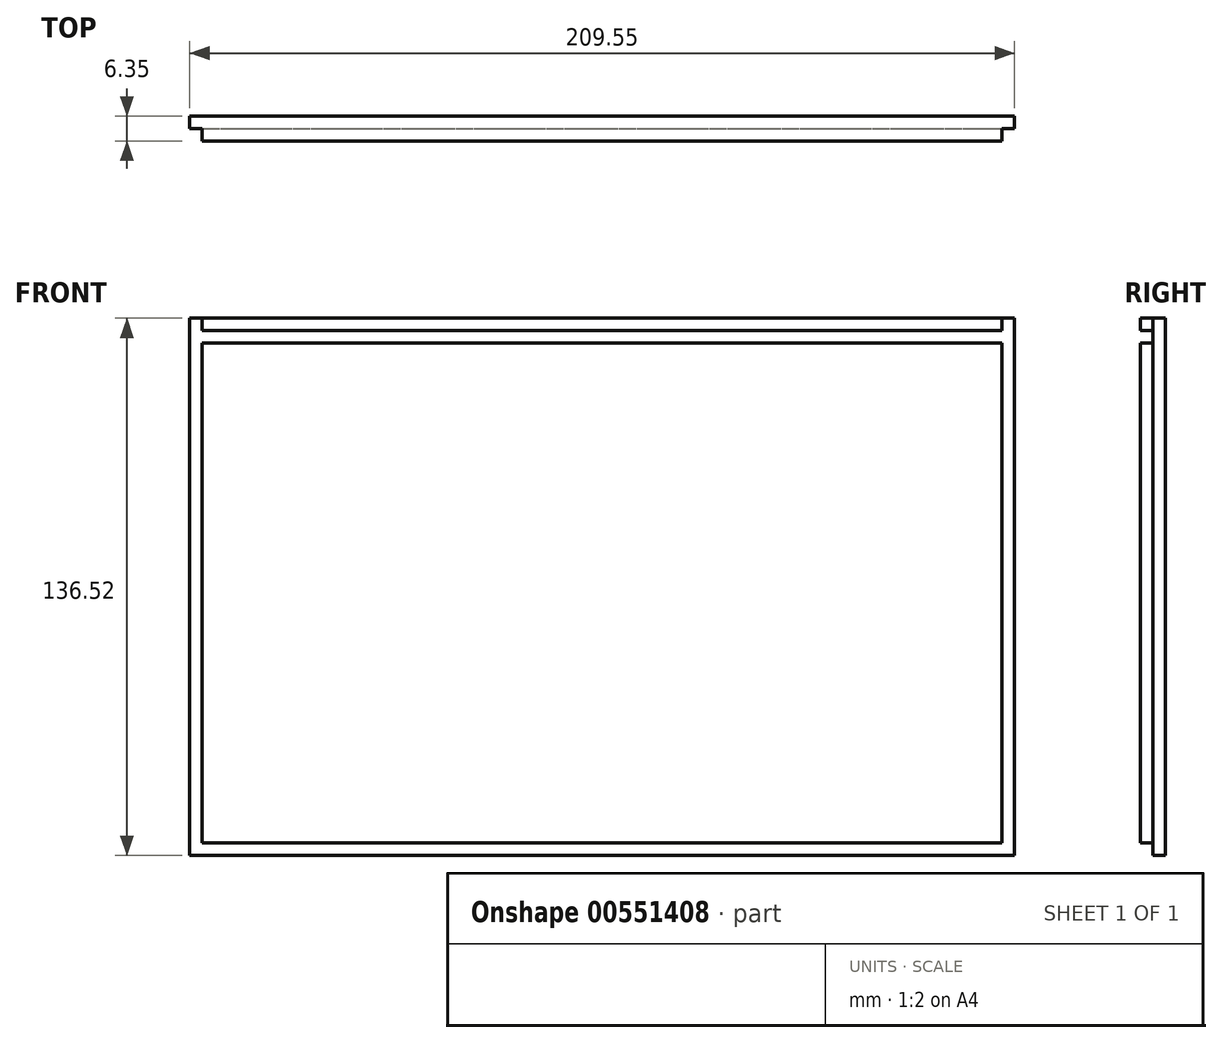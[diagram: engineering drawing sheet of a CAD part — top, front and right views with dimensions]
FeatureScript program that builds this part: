
annotation { "Feature Type Name" : "Feature", "Feature Type Description" : "" }
export const myFeature = defineFeature(function(context is Context, id is Id, definition is map)
    precondition{}
    {
        {
            var Q0;
            Q0=qCreatedBy(makeId("Front.planeOp"),FACE);
            var sketch = newSketch(context, id + "F0", { "sketchPlane" : qUnion([Q0])});
            skLineSegment(sketch, "E0.bottom", {"start": v(101.6, 63.5) * mm, "end": v(-101.6, 63.5) * mm});
            skLineSegment(sketch, "E0.top", {"start": v(101.6, -63.5) * mm, "end": v(-101.6, -63.5) * mm});
            skLineSegment(sketch, "E0.left", {"start": v(101.6, 63.5) * mm, "end": v(101.6, -63.5) * mm});
            skLineSegment(sketch, "E0.right", {"start": v(-101.6, 63.5) * mm, "end": v(-101.6, -63.5) * mm});
            skPoint(sketch, "E0.middle", {"position": v(0, 0) * mm});
            skPoint(sketch, "E1.endSnap0", {"position": v(-101.6, 0) * mm});
            skPoint(sketch, "E2.endSnap0", {"position": v(0, 63.5) * mm});
            skPoint(sketch, "E3.endSnap0", {"position": v(0, -63.5) * mm});
            skSolve(sketch);
        }
        {
            var Q0;
            Q0 = qSketchRegion(id + "F0", true);
            extrude(context, id + "F1", {"entities" : qUnion([Q0]), "depth" : 6.35 * mm, "offsetDistance" : 25.4 * mm});
        }
        {
            var Q0;
            Q0=makeQuery(id+"F1.opExtrude","SWEPT_FACE",FACE,{"disambiguationData":[OSD([sQuery(id+"F0.wireOp",EDGE,"E0.left")])]});
            var sketch = newSketch(context, id + "F2", { "sketchPlane" : qUnion([Q0])});
            skLineSegment(sketch, "E4", {"start": v(0, 63.5) * mm, "end": v(-3.18, 63.5) * mm});
            skLineSegment(sketch, "E5", {"start": v(-3.18, 63.5) * mm, "end": v(-3.18, 66.68) * mm});
            skLineSegment(sketch, "E6", {"start": v(-3.18, 66.68) * mm, "end": v(-6.35, 66.68) * mm});
            skLineSegment(sketch, "E7", {"start": v(-6.35, 66.68) * mm, "end": v(-6.35, 69.85) * mm});
            skLineSegment(sketch, "E8", {"start": v(-6.35, 69.85) * mm, "end": v(0, 69.85) * mm});
            skLineSegment(sketch, "E9", {"start": v(0, 69.85) * mm, "end": v(0, 63.5) * mm});
            skLineSegment(sketch, "E10", {"start": v(-30.08, 0) * mm, "end": v(17.13, 0) * mm, "construction": true});
            skPoint(sketch, "E10.endSnap0", {"position": v(-6.35, 0) * mm});
            skLineSegment(sketch, "E11.MirrorCS", {"start": v(0, -66.68) * mm, "end": v(0, -63.5) * mm});
            skLineSegment(sketch, "E12.MirrorCS", {"start": v(-3.18, -63.5) * mm, "end": v(-3.18, -66.68) * mm});
            skLineSegment(sketch, "E13.MirrorCS", {"start": v(0, -63.5) * mm, "end": v(-3.18, -63.5) * mm});
            skLineSegment(sketch, "E14", {"start": v(-3.18, -66.68) * mm, "end": v(0, -66.68) * mm});
            skPoint(sketch, "E15.end.orphan", {"position": v(0, -69.85) * mm});
            skPoint(sketch, "E15.start.orphan", {"position": v(-3.18, -69.85) * mm});
            skSolve(sketch);
        }
        {
            var Q0;
            Q0=makeQuery(id+"F2.imprint","IMPRINT",FACE,{"disambiguationData":[TD([[makeQuery(id+"F2.imprint","IMPRINT",EDGE,{"derivedFrom":sQuery(id+"F2.wireOp",EDGE,"E4")}),1.0]])]});
            var Q1;
            Q1=makeQuery(id+"F2.imprint","IMPRINT",FACE,{"disambiguationData":[TD([[makeQuery(id+"F2.imprint","IMPRINT",EDGE,{"derivedFrom":sQuery(id+"F2.wireOp",EDGE,"E11.MirrorCS")}),1.0]])]});
            extrude(context, id + "F3", {"entities" : qUnion([Q0, Q1]), "operationType" : NewBodyOperationType.ADD, "oppositeDirection" : true, "depth" : 203.2 * mm, "offsetDistance" : 25.4 * mm});
        }
        {
            var Q0;
            Q0=makeQuery(id+"F3.opExtrude","SWEPT_FACE",FACE,{"disambiguationData":[OSD([sQuery(id+"F2.wireOp",EDGE,"E14")])]});
            var sketch = newSketch(context, id + "F4", { "sketchPlane" : qUnion([Q0])});
            skLineSegment(sketch, "E16", {"start": v(-101.6, 3.18) * mm, "end": v(-104.78, 3.18) * mm});
            skLineSegment(sketch, "E17", {"start": v(-104.78, 3.18) * mm, "end": v(-104.78, 0) * mm});
            skLineSegment(sketch, "E18", {"start": v(-104.78, 0) * mm, "end": v(-101.6, 0) * mm});
            skLineSegment(sketch, "E19", {"start": v(0, 13.66) * mm, "end": v(0, -12.32) * mm, "construction": true});
            skPoint(sketch, "E19.endSnap0", {"position": v(0, 3.18) * mm});
            skLineSegment(sketch, "E20.MirrorCS", {"start": v(104.78, 3.18) * mm, "end": v(104.78, 0) * mm});
            skLineSegment(sketch, "E21.MirrorCS", {"start": v(101.6, 3.18) * mm, "end": v(104.78, 3.18) * mm});
            skLineSegment(sketch, "E22.MirrorCS", {"start": v(104.78, 0) * mm, "end": v(101.6, 0) * mm});
            skSolve(sketch);
        }
        {
            var Q0;
            Q0=makeQuery(id+"F4.imprint","IMPRINT",FACE,{"disambiguationData":[TD([[makeQuery(id+"F4.imprint","IMPRINT",EDGE,{"derivedFrom":sQuery(id+"F4.wireOp",EDGE,"E16")}),1.0]])]});
            var Q1;
            Q1=makeQuery(id+"F4.imprint","IMPRINT",FACE,{"disambiguationData":[TD([[makeQuery(id+"F4.imprint","IMPRINT",EDGE,{"derivedFrom":sQuery(id+"F4.wireOp",EDGE,"E20.MirrorCS")}),-1.0]])]});
            extrude(context, id + "F5", {"entities" : qUnion([Q0, Q1]), "operationType" : NewBodyOperationType.ADD, "oppositeDirection" : true, "depth" : 136.53 * mm, "offsetDistance" : 25.4 * mm});
        }
    });
